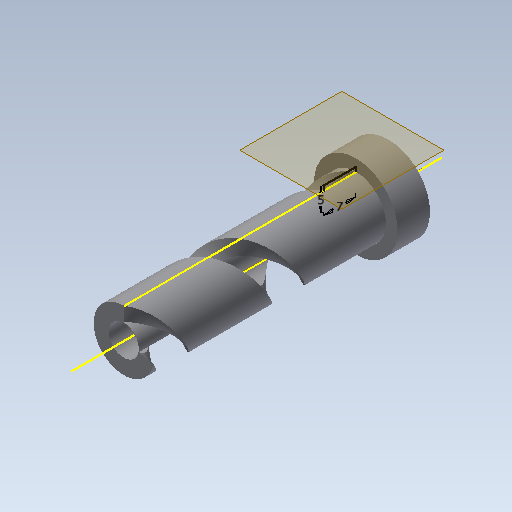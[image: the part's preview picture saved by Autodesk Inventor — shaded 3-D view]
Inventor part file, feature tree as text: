
AUTODESK INVENTOR PART (.ipt)
format: ipt  version: 2020.1 (Build 241239000, 239)  size: 217,088 bytes
history: native  units: mm
features: sketch x8, extrude x7, plane x1, other x1, helix x1
ambient origin geometry x8: Origin, YZ Plane, XZ Plane, XY Plane, X Axis, Y Axis, Z Axis, Center Point
bodies: Solid1 (feature_tree)
feature tree (18):
  extrude  "Extrusion1"  Depth=3.0mm
  extrude  "Extrusion2"  Depth=18.0mm
  extrude  "Extrusion3"  Depth=7.0mm
  extrude  "Extrusion5"  Depth=1.0mm
  plane  "Work Plane1"
  extrude  "Extrusion8"  Depth=6.5mm
  sketch  "Sketch9"  dims[d34=12.0mm d44=6.0mm]
  other  "Work Axis1"
  helix  "Coil2"  [1 undecoded]
  extrude  "Extrusión9"  Depth=6.0mm
  extrude  "Extrusión10"  Depth=5.0mm
  sketch  "Sketch1"  dims[d0=6.0mm d1=3.0mm]
  sketch  "Sketch2"  dims[d2=80.0mm d4=360.0deg d6=18.0mm]
  sketch  "Sketch3"  dims[d7=7.0mm d8=0.0mm d9=13.0mm]
  sketch  "Sketch5"  dims[d10=1.0mm d11=0.0mm d12=13.0mm]
  sketch  "Sketch8"  dims[d13=50.0mm d14=0.0mm d25=6.5mm d26=6.0mm d27=0.0mm]
  sketch  "Boceto13"  dims[d45=4.5mm d46=0.0mm d61=5.0mm]
  sketch  "Boceto14"  dims[d62=7.0mm d63=25.0mm d64=50.0mm d65=40.0mm d66=0.174533mm d67=90.0deg d68=90.0deg d69=0.0mm d70=0.0mm d72=7.0mm d73=0.0mm d74=2.0mm d75=0.0mm]
note: 1 required parameter value undecoded (feature->parameter linkage not recoverable at this tier; creation-order binding heuristic only, values carry confidence <= 0.55)
